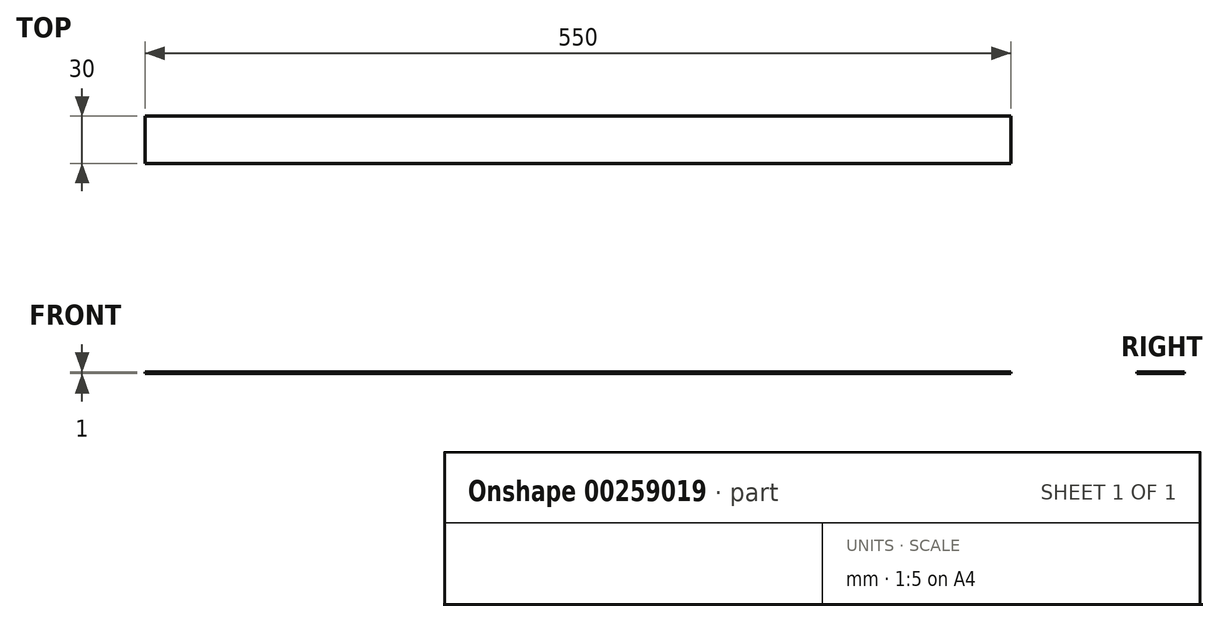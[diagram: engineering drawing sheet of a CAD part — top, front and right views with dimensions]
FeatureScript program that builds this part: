
annotation { "Feature Type Name" : "Feature", "Feature Type Description" : "" }
export const myFeature = defineFeature(function(context is Context, id is Id, definition is map)
    precondition{}
    {
        {
            var Q0;
            Q0=qCreatedBy(makeId("Right.planeOp"),FACE);
            var sketch = newSketch(context, id + "F0", { "sketchPlane" : qUnion([Q0])});
            skLineSegment(sketch, "E0.bottom", {"start": v(15, -0.5) * mm, "end": v(-15, -0.5) * mm});
            skLineSegment(sketch, "E0.top", {"start": v(15, 0.5) * mm, "end": v(-15, 0.5) * mm});
            skLineSegment(sketch, "E0.left", {"start": v(15, -0.5) * mm, "end": v(15, 0.5) * mm});
            skLineSegment(sketch, "E0.right", {"start": v(-15, -0.5) * mm, "end": v(-15, 0.5) * mm});
            skPoint(sketch, "E0.middle", {"position": v(0, 0) * mm});
            skSolve(sketch);
        }
        {
            var Q0;
            Q0 = qSketchRegion(id + "F0", true);
            extrude(context, id + "F1", {"entities" : qUnion([Q0]), "depth" : 550 * mm, "offsetDistance" : 25 * mm, "symmetric" : true});
        }
    });
